# Revit family: VLMF-REY-1-xxWSxxxRAx
name_source: partatom
category: Leuchten
units: mm (PartAtom-declared; Revit-internal decimal feet)

## family parameters
Basisbauteil = Fläche
Beim Laden mit Abzugskörper schneiden = Nein
Bemaßung runder Anschluss = Durchmesser verwenden
Gemeinsam genutzt = Nein
Lichtquelle = Ja
OmniClass-Nummer = 23.80.70.11
OmniClass-Titel = Luminaries for Internal Lighting
Raumberechnungspunkt = Nein
Teiletyp = Normal

## types (6) — shared parameters
Baugruppenkennzeichen = D5020200
Datei für fotometrisches Netz = REY-1 DAFWS840RA0650.IES
Emissionsform beim Rendern sichtbar = Nein
Farbfilter = 16777215
Farbtemperaturverschiebung bei Dämpfen der Lampe = <Keine Auswahl>
Hersteller = RIDI Leuchten GmbH
Lampe = LED
Neigungswinkel = 90.00°
Scheinlast = 53 VA
URL = www.ridi.de
Von Breite des Rechtecks ausssenden = 219 mm  [stored 0.718504 ft]
Von Länge des Rechtecks aussenden = 48 mm  [stored 0.15748 ft]
brand = RIDI
conformity mark = CE
electrical safety class = 1
height = 135 mm  [stored 0.442913 ft]
ingress protection (IP) code = IP20
length = 500 mm  [stored 1.64042 ft]
nominal frequency = 50-60Hz
nominal voltage = 230
rated input power = 53
voltage type (AC, DC, UC) = AC
weight = 1,37 kg
width = 76 mm  [stored 0.249344 ft]
zero-valued in all types: Vorgabe-Ansicht

## per-type parameters (varying)
| type | Modell |
| VLMF-REY-1 NDWS830RA0650 | 0322037//691 |
| VLMF-REY-1 DAWS830RA0650 | 0332037//691 |
| VLMF-REY-1 NDWS840RA0650 | 0322038//691 |
| VLMF-REY-1 DAWS840RA0650 | 0332038//691 |
| VLMF-REY-1 NDWS930RA0550 | 0322042//691 |
| VLMF-REY-1 DAWS930RA0550 | 0332042//691 |

note: column(s) folded — value = type name in every type: product name

note: [stored X ft] marks values corroborated as IEEE doubles in the binary element streams (Revit-internal decimal feet)
